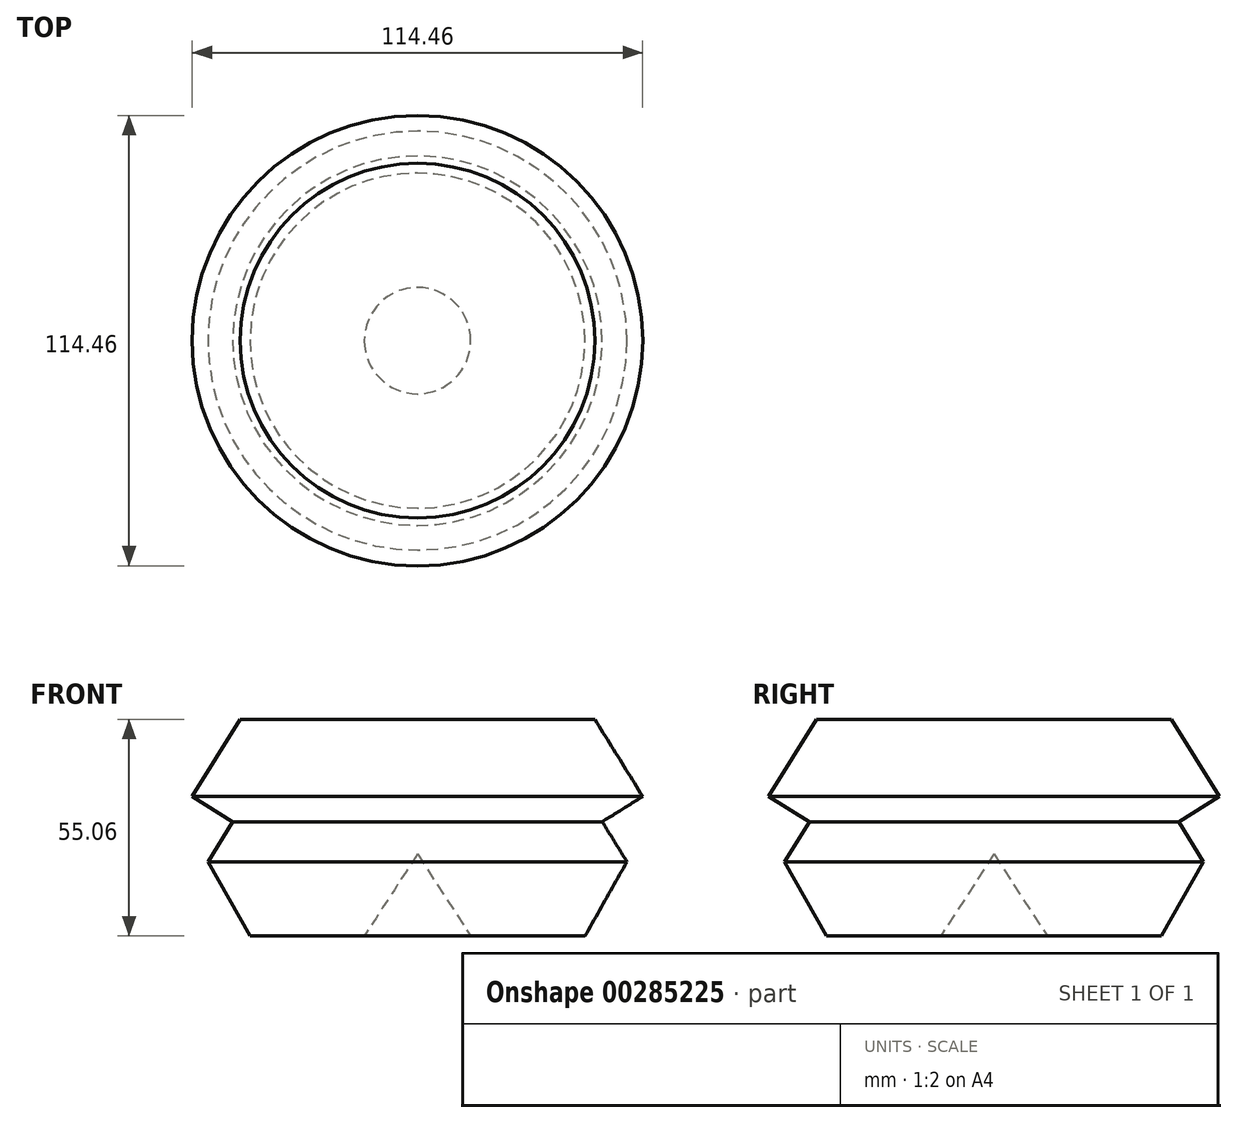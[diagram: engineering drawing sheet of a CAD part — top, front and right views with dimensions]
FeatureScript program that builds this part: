
annotation { "Feature Type Name" : "Feature", "Feature Type Description" : "" }
export const myFeature = defineFeature(function(context is Context, id is Id, definition is map)
    precondition{}
    {
        {
            var Q0;
            Q0=qCreatedBy(makeId("Front.planeOp"),FACE);
            var sketch = newSketch(context, id + "F0", { "sketchPlane" : qUnion([Q0])});
            skLineSegment(sketch, "E0", {"start": v(0, 20.84) * mm, "end": v(-13.52, 0) * mm});
            skLineSegment(sketch, "E1", {"start": v(-13.52, 0) * mm, "end": v(-42.55, 0) * mm});
            skLineSegment(sketch, "E2", {"start": v(-42.55, 0) * mm, "end": v(-53.22, 18.91) * mm});
            skLineSegment(sketch, "E3", {"start": v(-53.22, 18.91) * mm, "end": v(-46.93, 29.06) * mm});
            skLineSegment(sketch, "E4", {"start": v(-46.93, 29.06) * mm, "end": v(-57.23, 35.45) * mm});
            skLineSegment(sketch, "E5", {"start": v(-57.23, 35.45) * mm, "end": v(-45.07, 55.06) * mm});
            skLineSegment(sketch, "E6", {"start": v(-45.07, 55.06) * mm, "end": v(0, 55.06) * mm});
            skLineSegment(sketch, "E7", {"start": v(0, 55.06) * mm, "end": v(0, 20.84) * mm});
            skSolve(sketch);
        }
        {
            var Q0;
            Q0=makeQuery(id+"F0.imprint","IMPRINT",FACE,{"disambiguationData":[TD([[makeQuery(id+"F0.imprint","IMPRINT",EDGE,{"derivedFrom":sQuery(id+"F0.wireOp",EDGE,"E0")}),-1.0]])]});
            var Q1;
            Q1=sQuery(id+"F0.wireOp",EDGE,"E7");
            revolve(context, id + "F1", {"entities" : qUnion([Q0]), "axis" : qUnion([Q1]), "revolveType" : RevolveType.FULL});
        }
        {
            var Q0;
            Q0=makeQuery(id+"F1.opRevolve","SWEPT_FACE",FACE,{"disambiguationData":[OSD([sQuery(id+"F0.wireOp",EDGE,"E6")])]});
            var sketch = newSketch(context, id + "F2", { "sketchPlane" : qUnion([Q0])});
            skCircle(sketch, "E8.cCircle", {"center": v(0, 0) * mm, "radius": 35.93 * mm, "construction": true});
            skLineSegment(sketch, "E8.0", {"start": v(-41.49, -0.7) * mm, "end": v(-21.35, 35.58) * mm});
            skLineSegment(sketch, "E8.1", {"start": v(-21.35, 35.58) * mm, "end": v(20.14, 36.28) * mm});
            skLineSegment(sketch, "E8.2", {"start": v(20.14, 36.28) * mm, "end": v(41.49, 0.7) * mm});
            skLineSegment(sketch, "E8.3", {"start": v(41.49, 0.7) * mm, "end": v(21.35, -35.58) * mm});
            skLineSegment(sketch, "E8.4", {"start": v(21.35, -35.58) * mm, "end": v(-20.14, -36.28) * mm});
            skLineSegment(sketch, "E8.5", {"start": v(-20.14, -36.28) * mm, "end": v(-41.49, -0.7) * mm});
            skPoint(sketch, "E8.0.midPoint", {"position": v(-31.42, 17.44) * mm});
            skSolve(sketch);
        }
        {
            var Q0;
            Q0=makeQuery(id+"F2.imprint","IMPRINT",FACE,{"disambiguationData":[TD([[makeQuery(id+"F2.imprint","IMPRINT",EDGE,{"derivedFrom":sQuery(id+"F2.wireOp",EDGE,"E8.0")}),-1.0]])]});
            extrude(context, id + "F3", {"entities" : qUnion([Q0]), "operationType" : NewBodyOperationType.ADD, "oppositeDirection" : true, "depth" : 31.43 * mm});
        }
    });
